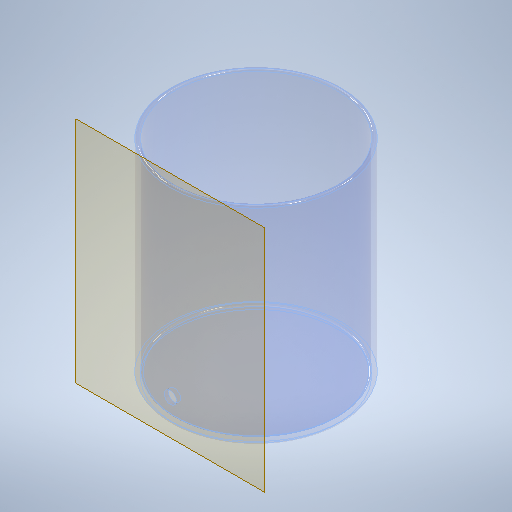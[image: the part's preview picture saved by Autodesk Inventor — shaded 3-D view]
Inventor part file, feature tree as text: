
AUTODESK INVENTOR PART (.ipt)
format: ipt  version: 2025.2 (Build 292293000, 293)  size: 306,176 bytes
history: native  units: mm
features: extrude x3, fillet x3, sketch x3, plane x1
ambient origin geometry x8: Origin, YZ Plane, XZ Plane, XY Plane, X Axis, Y Axis, Z Axis, Center Point
bodies: Solid1 (feature_tree)
feature tree (10):
  extrude  "Extrusion1"  Depth=2.0mm TaperAngle=0.0deg
  extrude  "Extrusion2"  Depth=1.0mm TaperAngle=0.0deg
  fillet  "Fillet1"  Radius=84.0mm
  fillet  "Fillet2"  Radius=2.0mm
  fillet  "Fillet3"  Radius=1.0mm
  extrude  "Extrusion3"  Depth=10.0mm
  plane  "Work Plane1"
  sketch  "Sketch1"  dims[d0=84.0mm d1=2.0mm d2=0.0mm]
  sketch  "Sketch2"  dims[d3=80.0mm d4=100.0mm d5=0.0mm d6=84.0mm d7=2.0mm d8=1.0mm]
  sketch  "Sketch3"  dims[d9=1.0mm d10=10.0mm d11=6.0mm d12=0.0mm d13=0.0mm]
